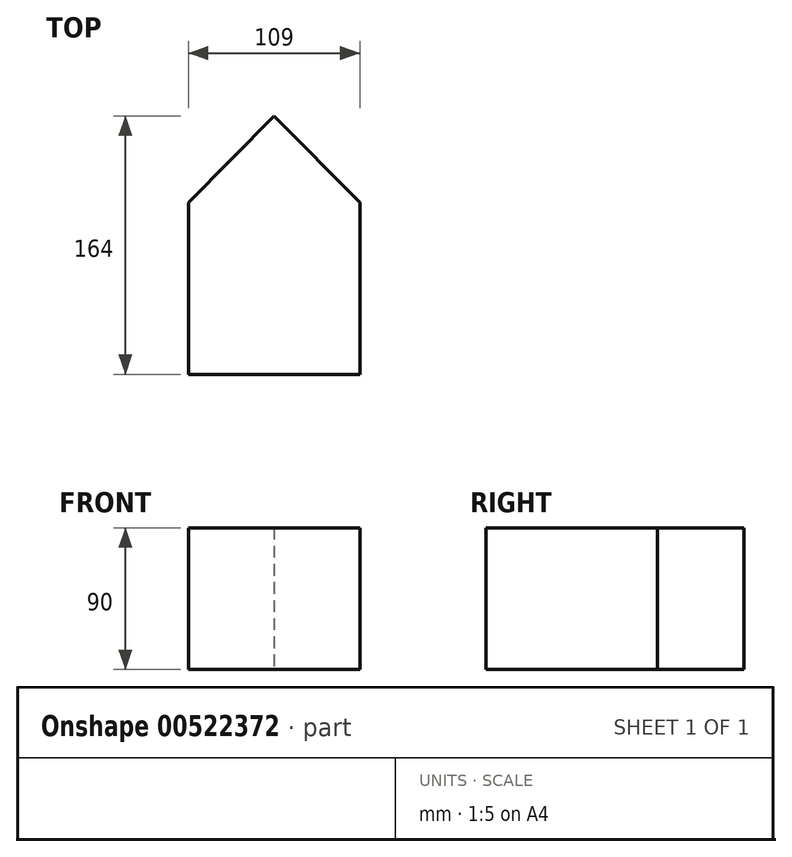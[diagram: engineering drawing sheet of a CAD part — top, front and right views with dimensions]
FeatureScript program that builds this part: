
annotation { "Feature Type Name" : "Feature", "Feature Type Description" : "" }
export const myFeature = defineFeature(function(context is Context, id is Id, definition is map)
    precondition{}
    {
        {
            var Q0;
            Q0=qCreatedBy(makeId("Top.planeOp"),FACE);
            var sketch = newSketch(context, id + "F0", { "sketchPlane" : qUnion([Q0])});
            skLineSegment(sketch, "E0.bottom", {"start": v(54.5, -54.5) * mm, "end": v(-54.5, -54.5) * mm});
            skLineSegment(sketch, "E0.left", {"start": v(54.5, -54.5) * mm, "end": v(54.5, 54.5) * mm});
            skLineSegment(sketch, "E0.right", {"start": v(-54.5, -54.5) * mm, "end": v(-54.5, 54.5) * mm});
            skPoint(sketch, "E0.middle", {"position": v(0, 0) * mm});
            skLineSegment(sketch, "E1", {"start": v(0, -54.5) * mm, "end": v(0, 109.5) * mm, "construction": true});
            skPoint(sketch, "E1.endSnap0", {"position": v(0, 54.5) * mm});
            skLineSegment(sketch, "E2", {"start": v(-54.5, 54.5) * mm, "end": v(0, 109.5) * mm});
            skLineSegment(sketch, "E3", {"start": v(54.5, 54.5) * mm, "end": v(0, 109.5) * mm});
            skSolve(sketch);
        }
        {
            var Q0;
            Q0=makeQuery(id+"F0.imprint","IMPRINT",FACE,{"disambiguationData":[TD([[makeQuery(id+"F0.imprint","IMPRINT",EDGE,{"derivedFrom":sQuery(id+"F0.wireOp",EDGE,"E0.bottom")}),-1.0]])]});
            extrude(context, id + "F1", {"entities" : qUnion([Q0]), "depth" : 90 * mm, "offsetDistance" : 25 * mm});
        }
    });
